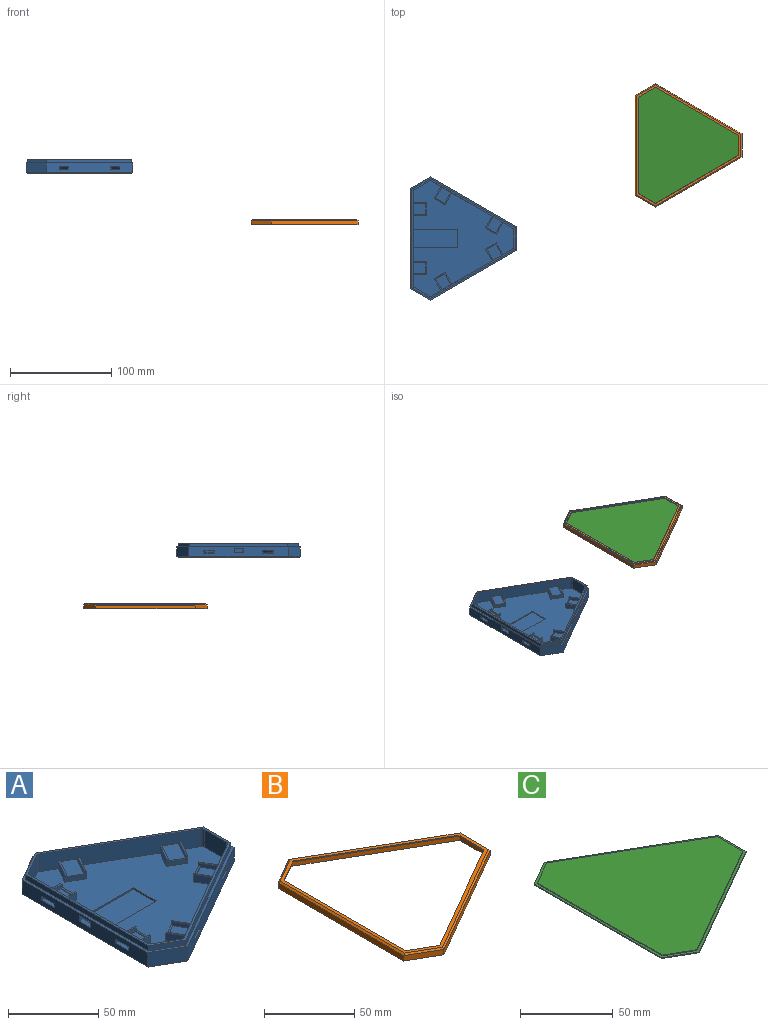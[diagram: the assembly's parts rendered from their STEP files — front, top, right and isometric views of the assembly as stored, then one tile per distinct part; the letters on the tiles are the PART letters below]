
ASSEMBLY  parts=3 mates=1
PART A: 108 faces, bbox 105.6x121.9x14 mm
  f0: plane 98.81x9.5mm, normal (-1,0,0), area 847.5mm2, adj f2,f3,f4,f15,f17,f22,f31,f42
  f1: plane 93.04x13mm, normal (1,0,0), area 972.9mm2, adj f32,f36,f44,f45,f80,f81,f82,f83
  f2: plane 15.45x10.4mm, normal (0,0,1), area 160.7mm2, adj f0,f3,f46,f92
  f3: plane 16.45x2.7mm, normal (0,1,0), area 43.9mm2, adj f0,f2,f45,f83,f84,f92,f93
  f4: plane 15.45x10.4mm, normal (0,0,1), area 160.7mm2, adj f0,f42,f43,f90
  f5: plane 18.58x16.73mm, normal (0,0,1), area 160.7mm2, adj f6,f13,f41,f78
  f6: plane 14.25x8.23mm, normal (-0.87,-0.5,0), area 43.9mm2, adj f5,f13,f40,f69,f70,f78,f79
  f7: plane 18.58x16.73mm, normal (0,0,1), area 160.7mm2, adj f13,f37,f39,f76
  f8: plane 18.58x16.73mm, normal (0,0,1), area 160.7mm2, adj f9,f11,f51,f64
  f9: plane 14.25x8.23mm, normal (0.87,-0.5,0), area 43.9mm2, adj f8,f11,f50,f57,f61,f64,f65
  f10: plane 18.58x16.73mm, normal (0,0,1), area 160.7mm2, adj f11,f47,f48,f62
  f11: plane 85.57x49.41mm, normal (0.5,0.87,0), area 882.6mm2, adj f8,f9,f10,f16,f17,f23,f31,f47
  f12: plane 80.57x46.52mm, normal (-0.5,-0.87,0), area 990mm2, adj f32,f36,f49,f50,f52,f53,f54,f55
  f13: plane 85.57x49.41mm, normal (0.5,-0.87,0), area 882.6mm2, adj f5,f6,f7,f15,f16,f19,f31,f37
  f14: plane 80.57x46.52mm, normal (-0.5,0.87,0), area 990mm2, adj f32,f36,f38,f40,f66,f67,f68,f69
  f15: plane 20x11.55mm, normal (-0.5,-0.87,0), area 219.4mm2, adj f0,f13,f20,f31
  f16: plane 23.09x9.5mm, normal (1,0,0), area 219.4mm2, adj f11,f13,f21,f31
  f17: plane 20x11.55mm, normal (-0.5,0.87,0), area 219.4mm2, adj f0,f11,f24,f31
  f18: plane 119.6x103.57mm, normal (0,0,-1), area 8049mm2, adj f19,f20,f21,f22,f23,f24
  f19: plane 85.57x49.98mm, normal (0.35,-0.61,-0.71), area 138.9mm2, adj f13,f18,f20,f21
  f20: plane 20x12.12mm, normal (-0.35,-0.61,-0.71), area 31.8mm2, adj f15,f18,f19,f22
  f21: plane 23.09x1mm, normal (0.71,0,-0.71), area 31.8mm2, adj f16,f18,f19,f23
  f22: plane 98.81x1mm, normal (-0.71,0,-0.71), area 138.9mm2, adj f0,f18,f20,f24
  f23: plane 85.57x49.98mm, normal (0.35,0.61,-0.71), area 138.9mm2, adj f11,f18,f21,f24
  f24: plane 20x12.12mm, normal (-0.35,0.61,-0.71), area 31.8mm2, adj f17,f18,f22,f23
  f25: plane 84.02x48.51mm, normal (0.5,0.87,0), area 339.6mm2, adj f26,f30,f31,f36
  f26: plane 21.3x3.5mm, normal (1,0,0), area 74.6mm2, adj f25,f27,f31,f36
  f27: plane 84.02x48.51mm, normal (0.5,-0.87,0), area 339.6mm2, adj f26,f28,f31,f36
  f28: plane 18.45x10.65mm, normal (-0.5,-0.87,0), area 74.6mm2, adj f27,f29,f31,f36
  f29: plane 97.02x3.5mm, normal (-1,0,0), area 339.6mm2, adj f28,f30,f31,f36
  f30: plane 18.45x10.65mm, normal (-0.5,0.87,0), area 74.6mm2, adj f25,f29,f31,f36
  f31: plane 121.91x105.57mm, normal (0,0,1), area 558.5mm2, adj f0,f11,f13,f15,f16,f17,f25,f26
  f32: plane 114.36x99.57mm, normal (0,0,1), area 5551.3mm2, adj f1,f12,f14,f33,f34,f35,f53,f54
  f33: plane 15x12mm, normal (0.5,-0.87,0), area 207.8mm2, adj f32,f36,f103,f104
  f34: plane 15x12mm, normal (0.5,0.87,0), area 207.8mm2, adj f32,f36,f105,f106
  f35: plane 17.32x12mm, normal (-1,0,0), area 207.8mm2, adj f32,f36,f102,f107
  f36: plane 118.33x102.47mm, normal (0,0,1), area 508.7mm2, adj f1,f12,f14,f25,f26,f27,f28,f29
  f37: plane 14.25x8.23mm, normal (-0.87,-0.5,0), area 43.9mm2, adj f7,f13,f38,f74,f75,f76,f77
  f38: plane 10.51x7.8mm, normal (0,0,-1), area 31.2mm2, adj f13,f14,f37,f39
  f39: plane 14.25x8.23mm, normal (0.87,0.5,0), area 43.9mm2, adj f7,f13,f38,f73,f75,f76,f77
  f40: plane 10.51x7.8mm, normal (0,0,-1), area 31.2mm2, adj f6,f13,f14,f41
  f41: plane 14.25x8.23mm, normal (0.87,0.5,0), area 43.9mm2, adj f5,f13,f40,f68,f70,f78,f79
  f42: plane 16.45x2.7mm, normal (0,-1,0), area 43.9mm2, adj f0,f4,f44,f87,f89,f90,f91
  f43: plane 16.45x2.7mm, normal (0,1,0), area 43.9mm2, adj f0,f4,f44,f88,f89,f90,f91
  f44: plane 10.4x3mm, normal (0,0,-1), area 31.2mm2, adj f0,f1,f42,f43
  f45: plane 10.4x3mm, normal (0,0,-1), area 31.2mm2, adj f0,f1,f3,f46
  f46: plane 16.45x2.7mm, normal (0,-1,0), area 43.9mm2, adj f0,f2,f45,f82,f84,f92,f93
  f47: plane 14.25x8.23mm, normal (-0.87,0.5,0), area 43.9mm2, adj f10,f11,f49,f55,f56,f62,f63
  f48: plane 14.25x8.23mm, normal (0.87,-0.5,0), area 43.9mm2, adj f10,f11,f49,f52,f56,f62,f63
  f49: plane 10.51x7.8mm, normal (0,0,-1), area 31.2mm2, adj f11,f12,f47,f48
  f50: plane 10.51x7.8mm, normal (0,0,-1), area 31.2mm2, adj f9,f11,f12,f51
  f51: plane 14.25x8.23mm, normal (-0.87,0.5,0), area 43.9mm2, adj f8,f11,f50,f60,f61,f64,f65
  f52: plane 12.15x7.59mm, normal (0,0,1), area 13.5mm2, adj f12,f48,f53,f56
  f53: plane 11.65x6.73mm, normal (-0.87,0.5,0), area 68.6mm2, adj f12,f32,f52,f56
  f54: plane 11.65x6.73mm, normal (0.87,-0.5,0), area 68.6mm2, adj f12,f32,f55,f56
  f55: plane 12.15x7.59mm, normal (0,0,1), area 13.4mm2, adj f12,f47,f54,f56
  f56: plane 10.74x6.2mm, normal (-0.5,-0.87,0), area 40.4mm2, adj f32,f47,f48,f52,f53,f54,f55,f63
  f57: plane 12.15x7.59mm, normal (0,0,1), area 13.5mm2, adj f9,f12,f58,f61
  f58: plane 11.65x6.73mm, normal (-0.87,0.5,0), area 68.6mm2, adj f12,f32,f57,f61
  f59: plane 11.65x6.73mm, normal (0.87,-0.5,0), area 68.6mm2, adj f12,f32,f60,f61
  f60: plane 12.15x7.59mm, normal (0,0,1), area 13.4mm2, adj f12,f51,f59,f61
  f61: plane 10.74x6.2mm, normal (-0.5,-0.87,0), area 40.4mm2, adj f9,f32,f51,f57,f58,f59,f60,f65
  f62: plane 9.01x5.2mm, normal (0.5,0.87,0), area 5.2mm2, adj f10,f47,f48,f63
  f63: plane 9.51x6.07mm, normal (0,0,1), area 10.4mm2, adj f47,f48,f56,f62
  f64: plane 9.01x5.2mm, normal (0.5,0.87,0), area 5.2mm2, adj f8,f9,f51,f65
  f65: plane 9.51x6.07mm, normal (0,0,1), area 10.4mm2, adj f9,f51,f61,f64
  f66: plane 11.65x6.73mm, normal (0.87,0.5,0), area 68.6mm2, adj f14,f32,f69,f70
  f67: plane 11.65x6.73mm, normal (-0.87,-0.5,0), area 68.6mm2, adj f14,f32,f68,f70
  f68: plane 12.15x7.59mm, normal (0,0,1), area 13.5mm2, adj f14,f41,f67,f70
  f69: plane 12.15x7.59mm, normal (0,0,1), area 13.4mm2, adj f6,f14,f66,f70
  f70: plane 10.74x6.2mm, normal (-0.5,0.87,0), area 40.4mm2, adj f6,f32,f41,f66,f67,f68,f69,f79
  f71: plane 11.65x6.73mm, normal (0.87,0.5,0), area 68.6mm2, adj f14,f32,f74,f75
  f72: plane 11.65x6.73mm, normal (-0.87,-0.5,0), area 68.6mm2, adj f14,f32,f73,f75
  f73: plane 12.15x7.59mm, normal (0,0,1), area 13.5mm2, adj f14,f39,f72,f75
  f74: plane 12.15x7.59mm, normal (0,0,1), area 13.5mm2, adj f14,f37,f71,f75
  f75: plane 10.74x6.2mm, normal (-0.5,0.87,0), area 40.4mm2, adj f32,f37,f39,f71,f72,f73,f74,f77
  f76: plane 9.01x5.2mm, normal (0.5,-0.87,0), area 5.2mm2, adj f7,f37,f39,f77
  f77: plane 9.51x6.07mm, normal (0,0,1), area 10.4mm2, adj f37,f39,f75,f76
  f78: plane 9.01x5.2mm, normal (0.5,-0.87,0), area 5.2mm2, adj f5,f6,f41,f79
  f79: plane 9.51x6.07mm, normal (0,0,1), area 10.4mm2, adj f6,f41,f70,f78
  f80: plane 13.45x5.1mm, normal (0,-1,0), area 68.6mm2, adj f1,f32,f83,f84
  f81: plane 13.45x5.1mm, normal (0,1,0), area 68.6mm2, adj f1,f32,f82,f84
  f82: plane 13.45x1mm, normal (0,0,1), area 13.5mm2, adj f1,f46,f81,f84
  f83: plane 13.45x1mm, normal (0,0,1), area 13.4mm2, adj f1,f3,f80,f84
  f84: plane 12.4x5.1mm, normal (1,0,0), area 40.4mm2, adj f3,f32,f46,f80,f81,f82,f83,f93
  f85: plane 13.45x5.1mm, normal (0,-1,0), area 68.6mm2, adj f1,f32,f88,f89
  f86: plane 13.45x5.1mm, normal (0,1,0), area 68.6mm2, adj f1,f32,f87,f89
  f87: plane 13.45x1mm, normal (0,0,1), area 13.4mm2, adj f1,f42,f86,f89
  f88: plane 13.45x1mm, normal (0,0,1), area 13.5mm2, adj f1,f43,f85,f89
  f89: plane 12.4x5.1mm, normal (1,0,0), area 40.4mm2, adj f32,f42,f43,f85,f86,f87,f88,f91
  f90: plane 10.4x0.5mm, normal (-1,0,0), area 5.2mm2, adj f4,f42,f43,f91
  f91: plane 10.4x1mm, normal (0,0,1), area 10.4mm2, adj f42,f43,f89,f90
  f92: plane 10.4x0.5mm, normal (-1,0,0), area 5.2mm2, adj f2,f3,f46,f93
  f93: plane 10.4x1mm, normal (0,0,1), area 10.4mm2, adj f3,f46,f84,f92
  f94: plane 18x1mm, normal (-1,0,0), area 18mm2, adj f32,f95,f96,f97
  f95: plane 44x1mm, normal (0,-1,0), area 44mm2, adj f1,f32,f94,f97
  f96: plane 44x1mm, normal (0,1,0), area 44mm2, adj f1,f32,f94,f97
  f97: plane 44x18mm, normal (0,0,1), area 792mm2, adj f1,f94,f95,f96
  f98: plane 9x3mm, normal (0,0,1), area 27mm2, adj f0,f1,f99,f101
  f99: plane 3.9x3mm, normal (0,-1,0), area 11.7mm2, adj f0,f1,f98,f100
  f100: plane 9x3mm, normal (0,0,-1), area 27mm2, adj f0,f1,f99,f101
  f101: plane 3.9x3mm, normal (0,1,0), area 11.7mm2, adj f0,f1,f98,f100
  f102: cylinder r=2mm len=12mm, axis (0,0,1), area 25.1mm2, adj f12,f32,f35,f36
  f103: cylinder r=2mm len=12mm, axis (0,0,1), area 25.1mm2, adj f12,f32,f33,f36
  f104: cylinder r=2mm len=12mm, axis (0,0,1), area 25.1mm2, adj f1,f32,f33,f36
  f105: cylinder r=2mm len=12mm, axis (0,0,-1), area 25.1mm2, adj f1,f32,f34,f36
  f106: cylinder r=2mm len=12mm, axis (0,0,-1), area 25.1mm2, adj f14,f32,f34,f36
  f107: cylinder r=2mm len=12mm, axis (0,0,1), area 25.1mm2, adj f14,f32,f35,f36
PART B: 27 faces, bbox 105.6x121.9x4.7 mm
  f0: plane 82.57x47.67mm, normal (-0.5,-0.87,0), area 62mm2, adj f1,f5,f6,f7
  f1: plane 19.63x0.65mm, normal (-1,0,0), area 12.8mm2, adj f0,f2,f6,f7
  f2: plane 82.57x47.67mm, normal (-0.5,0.87,0), area 62mm2, adj f1,f3,f6,f7
  f3: plane 17x9.82mm, normal (0.5,0.87,0), area 12.8mm2, adj f2,f4,f6,f7
  f4: plane 95.35x0.65mm, normal (1,0,0), area 62mm2, adj f3,f5,f6,f7
  f5: plane 17x9.82mm, normal (0.5,-0.87,0), area 12.8mm2, adj f0,f4,f6,f7
  f6: plane 119.6x103.57mm, normal (0,0,1), area 703.7mm2, adj f0,f1,f2,f3,f4,f5,f21,f22
  f7: plane 118.56x102.67mm, normal (0,0,-1), area 543mm2, adj f0,f1,f2,f3,f4,f5,f13,f14
  f8: plane 20x11.55mm, normal (-0.5,0.87,0), area 84.3mm2, adj f9,f19,f20,f26
  f9: plane 98.81x3.65mm, normal (-1,0,0), area 360.7mm2, adj f8,f10,f20,f24
  f10: plane 20x11.55mm, normal (-0.5,-0.87,0), area 84.3mm2, adj f9,f11,f20,f22
  f11: plane 85.57x49.41mm, normal (0.5,-0.87,0), area 360.7mm2, adj f10,f12,f20,f21
  f12: plane 23.09x3.65mm, normal (1,0,0), area 84.3mm2, adj f11,f19,f20,f23
  f13: plane 84.12x48.57mm, normal (-0.5,-0.87,0), area 388.6mm2, adj f7,f14,f18,f20
  f14: plane 21.42x4mm, normal (-1,0,0), area 85.7mm2, adj f7,f13,f15,f20
  f15: plane 84.12x48.57mm, normal (-0.5,0.87,0), area 388.6mm2, adj f7,f14,f16,f20
  f16: plane 18.55x10.71mm, normal (0.5,0.87,0), area 85.7mm2, adj f7,f15,f17,f20
  f17: plane 97.14x4mm, normal (1,0,0), area 388.6mm2, adj f7,f16,f18,f20
  f18: plane 18.55x10.71mm, normal (0.5,-0.87,0), area 85.7mm2, adj f7,f13,f17,f20
  f19: plane 85.57x49.41mm, normal (0.5,0.87,0), area 360.7mm2, adj f8,f12,f20,f25
  f20: plane 121.91x105.57mm, normal (0,0,-1), area 523mm2, adj f8,f9,f10,f11,f12,f13,f14,f15
  f21: plane 85.57x49.98mm, normal (0.35,-0.61,0.71), area 138.9mm2, adj f6,f11,f22,f23
  f22: plane 20x12.12mm, normal (-0.35,-0.61,0.71), area 31.8mm2, adj f6,f10,f21,f24
  f23: plane 23.09x1mm, normal (0.71,0,0.71), area 31.8mm2, adj f6,f12,f21,f25
  f24: plane 98.81x1mm, normal (-0.71,0,0.71), area 138.9mm2, adj f6,f9,f22,f26
  f25: plane 85.57x49.98mm, normal (0.35,0.61,0.71), area 138.9mm2, adj f6,f19,f23,f26
  f26: plane 20x12.12mm, normal (-0.35,0.61,0.71), area 31.8mm2, adj f6,f8,f24,f25
PART C: 15 faces, bbox 102.5x118.3x1 mm
  f0: plane 16.85x9.73mm, normal (-0.5,-0.87,0), area 9.7mm2, adj f1,f5,f6,f13
  f1: plane 82.42x47.59mm, normal (0.5,-0.87,0), area 47.6mm2, adj f0,f2,f6,f13
  f2: plane 19.46x0.5mm, normal (1,0,0), area 9.7mm2, adj f1,f3,f6,f13
  f3: plane 82.42x47.59mm, normal (0.5,0.87,0), area 47.6mm2, adj f2,f4,f6,f13
  f4: plane 16.85x9.73mm, normal (-0.5,0.87,0), area 9.7mm2, adj f3,f5,f6,f13
  f5: plane 95.17x0.5mm, normal (-1,0,0), area 47.6mm2, adj f0,f4,f6,f13
  f6: plane 114.63x99.27mm, normal (0,0,1), area 7293.6mm2, adj f0,f1,f2,f3,f4,f5
  f7: plane 21.3x0.5mm, normal (1,0,0), area 10.7mm2, adj f8,f12,f13,f14
  f8: plane 84.02x48.51mm, normal (0.5,0.87,0), area 48.5mm2, adj f7,f9,f13,f14
  f9: plane 18.45x10.65mm, normal (-0.5,0.87,0), area 10.7mm2, adj f8,f10,f13,f14
  f10: plane 97.02x0.5mm, normal (-1,0,0), area 48.5mm2, adj f9,f11,f13,f14
  f11: plane 18.45x10.65mm, normal (-0.5,-0.87,0), area 10.7mm2, adj f10,f12,f13,f14
  f12: plane 84.02x48.51mm, normal (0.5,-0.87,0), area 48.5mm2, adj f7,f11,f13,f14
  f13: plane 118.33x102.47mm, normal (0,0,1), area 559.1mm2, adj f0,f1,f2,f3,f4,f5,f7,f8
  f14: plane 118.33x102.47mm, normal (0,0,-1), area 7852.7mm2, adj f7,f8,f9,f10,f11,f12
PLACE A t=(8.17,23.81,12.18)mm
PLACE B t=(230.69,115.94,-48.94)mm
PLACE C t=(230.44,116.13,-49.34)mm
MATE fastened B.f7 <-> C.f6  axis (0,0,1) through (191.83,163.61,-34.34)mm
